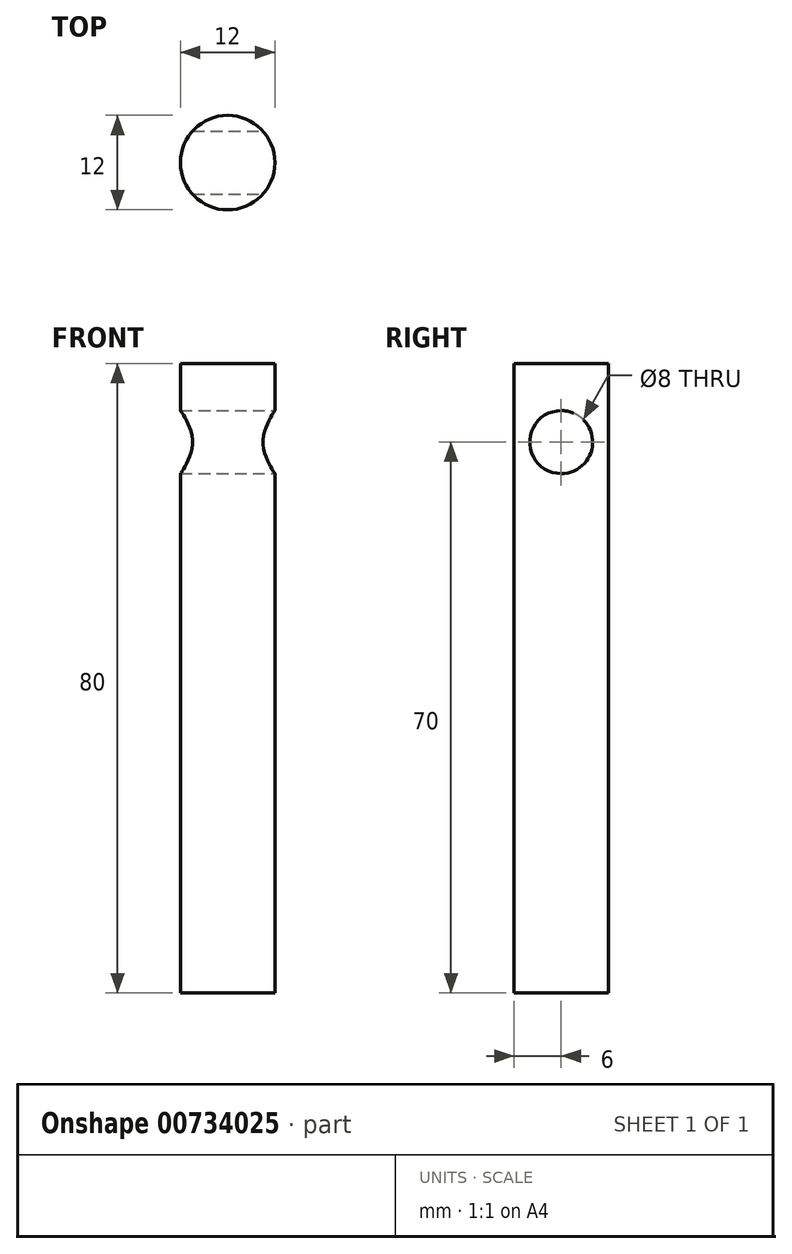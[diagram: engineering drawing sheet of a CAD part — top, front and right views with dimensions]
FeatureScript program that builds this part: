
annotation { "Feature Type Name" : "Feature", "Feature Type Description" : "" }
export const myFeature = defineFeature(function(context is Context, id is Id, definition is map)
    precondition{}
    {
        {
            var Q0;
            Q0=qCreatedBy(makeId("Top.planeOp"),FACE);
            var sketch = newSketch(context, id + "F0", { "sketchPlane" : qUnion([Q0])});
            skCircle(sketch, "E0", {"center": v(0, 0) * mm, "radius": 6 * mm});
            skSolve(sketch);
        }
        {
            var Q0;
            Q0 = qSketchRegion(id + "F0", true);
            extrude(context, id + "F1", {"entities" : qUnion([Q0]), "endBound" : BoundingType.SYMMETRIC, "depth" : 80 * mm, "offsetDistance" : 25 * mm});
        }
        {
            var Q0;
            Q0=qCreatedBy(makeId("Right.planeOp"),FACE);
            var sketch = newSketch(context, id + "F2", { "sketchPlane" : qUnion([Q0])});
            skCircle(sketch, "E1", {"center": v(0, 30) * mm, "radius": 4 * mm});
            skSolve(sketch);
        }
        {
            var Q0;
            Q0 = qSketchRegion(id + "F2", true);
            extrude(context, id + "F3", {"entities" : qUnion([Q0]), "operationType" : NewBodyOperationType.REMOVE, "endBound" : BoundingType.SYMMETRIC, "oppositeDirection" : true, "depth" : 25 * mm, "offsetDistance" : 25 * mm});
        }
    });
